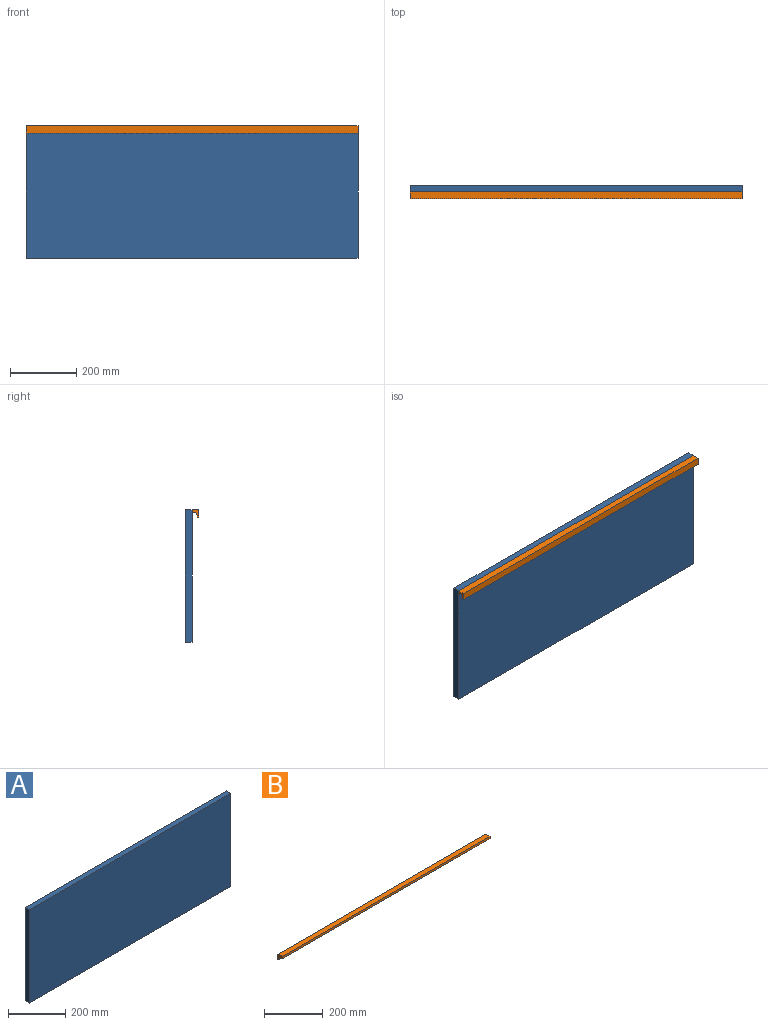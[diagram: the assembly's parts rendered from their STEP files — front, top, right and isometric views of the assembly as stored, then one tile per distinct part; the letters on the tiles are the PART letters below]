
ASSEMBLY  parts=2 mates=1
PART A: 6 faces, bbox 1000x20x400 mm
  f0: plane 400x20mm, normal (-1,0,0), area 8000mm2, adj f1,f3,f4,f5
  f1: plane 1000x20mm, normal (0,0,-1), area 20000mm2, adj f0,f2,f4,f5
  f2: plane 400x20mm, normal (1,0,0), area 8000mm2, adj f1,f3,f4,f5
  f3: plane 1000x20mm, normal (0,0,1), area 20000mm2, adj f0,f2,f4,f5
  f4: plane 1000x400mm, normal (0,-1,0), area 400000mm2, adj f0,f1,f2,f3
  f5: plane 1000x400mm, normal (0,1,0), area 400000mm2, adj f0,f1,f2,f3
PART B: 8 faces, bbox 1000x20x22.5 mm
  f0: plane 1000x22.47mm, normal (0,1,0), area 22471.9mm2, adj f1,f5,f6,f7
  f1: plane 1000x20mm, normal (0,0,1), area 20000mm2, adj f0,f2,f6,f7
  f2: plane 1000x8.99mm, normal (0,-1,0), area 8988.8mm2, adj f1,f3,f6,f7
  f3: plane 1000x11.01mm, normal (0,0,-1), area 11011.2mm2, adj f2,f4,f6,f7
  f4: plane 1000x13.48mm, normal (0,-0.91,-0.42), area 14879.1mm2, adj f3,f5,f6,f7
  f5: plane 1000x2.7mm, normal (0,0,-1), area 2696.6mm2, adj f0,f4,f6,f7
  f6: plane 22.47x20mm, normal (1,0,0), area 258.6mm2, adj f0,f1,f2,f3,f4,f5
  f7: plane 22.47x20mm, normal (-1,0,0), area 258.6mm2, adj f0,f1,f2,f3,f4,f5
PLACE A t=(18.02,-1.6,-33)mm
PLACE B rot(axis=(0,0,1),180deg) t=(518.02,-31.6,155.76)mm
MATE planar B.f7 <-> A.f2  axis (1,0,0) through (518.02,-21.6,167)mm
